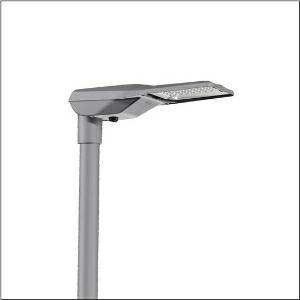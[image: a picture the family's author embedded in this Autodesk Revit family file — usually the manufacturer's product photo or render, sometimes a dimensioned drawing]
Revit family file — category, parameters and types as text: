
# Revit family: streetlight_sl_21_mini___p0_5a_5xe2v33r08gb_5767
name_source: partatom
category: Lighting Fixtures
units: mm (PartAtom-declared; Revit-internal decimal feet)

## family parameters
Cut with Voids When Loaded = No
Host = Face
Light Source = No
Part Type = Normal
Room Calculation Point = No
Round Connector Dimension = Use Diameter
Shared = No

## types (1)
- --- (1 x LED, 5840 lm, 40.4 W, 3000K)
    Apparent Load = 40 VA
    CIE Flux Codes = 37 73 96 100 100
    Color Rendering = 70
    Color Temperature = 3000K
    Default Elevation = 1800 mm
    Description = Streetlight SL 21 mini, mast luminaire, primary light control with lens, of PMMA, primary optical cover: cover, of toughened safety glass, transparent, light distribution: P0.5a, light emission: direct distribution, primary light characteristic: asymmetric, installation type: post-top, side-entry, LED, High Power LED, rated luminous flux: 5.840lm, luminous efficacy: 145lm/W, light colour: 730, colour temperature: 3000K, control gear: D4i, control: pre-setting: logarithmic dimming characteristic, flexible luminous flux parameterisation, time-dependent luminous flux control, constant luminous flux control, overheat protection, mains connection: 220..240V, AC, 50/60Hz, start of lifetime: 40W, end of service life: 41W, reduction: 19W, luminaire housing, of diecast aluminium, powder-coated, Siteco® metallic grey (DB 702S), corrosivity category C5 mid according to DIN EN ISO 12944, multi-level sealing system, sealing non-destructively replaceable, inclination adjustable: 0°, 5°, 10°, 15°, please order mast flange separately, length: 628mm, width: 235mm, height: 110mm, mast flange for spigot size: 42mm (side-entry): 5XC10008XM4, 60/48mm (side-entry/post-top): 5XC10108XM2, 76/60mm (side-entry/post-top): 5XC10108XM1, mounting height: 4..8m, Smart Interface below, protection rating (complete): IP66, insulation class (complete): insulation class II (safety insulation), certification: CE, ENEC, ENEC+, VDE, impact resistance: IK10, permissible operating ambient temperature for outdoor applications: -40..+50°C, standard-compliant lighting for roads and squares, packaging unit: 1 piece

Light Distribution: P0.5a
    Height = 110 mm
    Lamp = 1 x LED
    Lamp Light Flux = 5840 lm
    Lamp Power = 40.4 W
    Lamp count = 1
    Length = 625 mm
    Luminous efficacy = 145 lm/W
    Manufacturer = Siteco
    ModVariant = No
    Model = 5XE2V33R08GB
    Number of Poles = 1
    OnlyDefault = Yes
    Power Factor = 1
    Product Name = Streetlight SL 21 mini | P0.5a
    Product group = mast luminaire | pylon top
    ProductGroupID = 6100
    Protection Class = Protection class II
    Protection Degree = IP 66
    RLX_Detail_Level = 1
    RLX_Emergency_Light_Flux = 0 lm
    RLX_Emergency_Type = 0
    RLX_Emergency_Type_DB = No
    RlxData = <blob elided: 92681 chars, md5=4ff29e3e>
    Socket = socket
    Standby Power = 0 W
    System Light Flux = 5840 lm
    System Power = 40 W
    Type Comments = factory setting: luminous flux: 100 % | dim-lin: 254 | 812 mA
    Type Image = l_1003516.jpg
    URL = http://relux.com
    VarID = @adj_091101
    Voltage = 0 V
    Weight = 0.00 kg
    Width = 234 mm

## geometry (parser evidence)
native form markers: Blend x4, Sweep x12
no freeform markers — native parametric forms only
